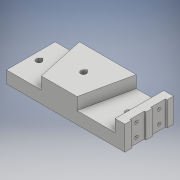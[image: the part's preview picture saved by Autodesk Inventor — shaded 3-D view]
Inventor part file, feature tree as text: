
AUTODESK INVENTOR PART (.ipt)
format: ipt  version: 2018 (Build 220112000, 112)  size: 235,520 bytes
history: native  units: mm
features: extrude x8, sketch x8, projected_geometry x2
ambient origin geometry x8: Origin, YZ Plane, XZ Plane, XY Plane, X Axis, Y Axis, Z Axis, Center Point
bodies: Solid1 (feature_tree)
feature tree (18):
  extrude  "Extrusion1"  Depth=30.0mm
  extrude  "Extrusion2"  Depth=22.0mm
  extrude  "Extrusion3"  Depth=15.0mm
  extrude  "Extrusion4"  Depth=7.5mm TaperAngle=0.0deg
  extrude  "Extrusion5"  Depth=5.0mm
  extrude  "Extrusion6"  Depth=7.5mm TaperAngle=0.0deg
  extrude  "Extrusion7"  Depth=6.0mm
  extrude  "Extrusion8"  Depth=3.0mm TaperAngle=0.0deg
  sketch  "Sketch1"  dims[d0=65.0mm d1=30.0mm]
  sketch  "Sketch2"  dims[d2=7.5mm d3=0.0mm d4=22.0mm]
  sketch  "Sketch3"  dims[d5=35.0mm d6=15.0mm]
  sketch  "Sketch4"  dims[d7=21.5mm d8=7.5mm d9=0.0mm]
  sketch  "Sketch5"  dims[d10=5.0mm d11=5.0mm]
  projected_geometry  "Projected Loop1"
  sketch  "Sketch6"  dims[d12=3.5mm d13=7.5mm d14=0.0mm]
  sketch  "Sketch7"  dims[d15=6.0mm d16=6.0mm]
  projected_geometry  "Projected Loop2"
  sketch  "Sketch8"  dims[d17=6.0mm d18=3.0mm d19=0.0mm d20=2.0mm d21=0.0mm d22=5.0mm d23=0.0mm d26=2.0mm d27=14.0mm d28=8.0mm d29=8.0mm d30=3.5mm d31=5.0mm d32=0.0mm d33=4.0mm d34=4.0mm d35=4.0mm d36=2.0mm d37=1.0mm d38=0.0mm d39=90.0deg d40=90.0deg d41=90.0deg d42=90.0deg d43=90.0deg d44=90.0deg d45=90.0deg]
